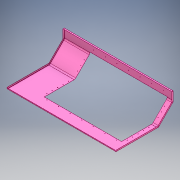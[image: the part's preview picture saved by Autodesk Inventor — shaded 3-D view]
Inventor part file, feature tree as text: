
AUTODESK INVENTOR PART (.ipt)
format: ipt  version: 2018 (Build 220112000, 112)  size: 371,200 bytes
history: native  units: mm
features: sheet_metal_op x13, sketch x10, other x5, hole x4, extrude x1
ambient origin geometry x8: Origin, YZ Plane, XZ Plane, XY Plane, X Axis, Y Axis, Z Axis, Center Point
bodies: Solid1 (feature_tree)
feature tree (33):
  sheet_metal_op  "Face1"
  sheet_metal_op  "Flange1"
  sheet_metal_op  "Flange2"
  extrude  "Extrusion1"  Depth=550.0mm
  sheet_metal_op  "Flange3"
  sheet_metal_op  "Flange4"
  sketch  "Sketch12"  dims[d13=1.6mm]
  sketch  "Sketch13"  dims[d14=0.8mm]
  sketch  "Sketch14"  dims[d15=3.2mm]
  hole  "Hole1"  [1 undecoded]
  hole  "Hole2"  [1 undecoded]
  hole  "Hole3"  [1 undecoded]
  hole  "Hole4"  [1 undecoded]
  sketch  "Sketch1"  dims[d0=1410.0mm d1=550.0mm]
  other  "Plate1"
  sketch  "Sketch2"  dims[d2=1.6mm d3=1.6mm]
  other  "Plate2"
  sheet_metal_op  "Bend1"
  sheet_metal_op  "Corner1"
  sketch  "Sketch3"  dims[d4=0.8mm d5=3.2mm]
  other  "Plate3"
  sheet_metal_op  "Bend2"
  sheet_metal_op  "Corner2"
  sketch  "Sketch4"  dims[d6=1.6mm d7=270.0mm d8=45.0deg d9=30.0mm]
  sketch  "Sketch5"  dims[d10=6.4mm d11=1.6mm]
  other  "Plate4"
  sheet_metal_op  "Bend3"
  sheet_metal_op  "Corner3"
  sketch  "Sketch6"  dims[d12=1.6mm]
  other  "Plate5"
  sheet_metal_op  "Bend4"
  sheet_metal_op  "Corner4"
  sketch  "Sketch15"  dims[d16=1.6mm d17=125.0mm d18=45.0deg d19=30.0mm d20=6.4mm d21=1.6mm d22=1.6mm d23=1000.0mm d24=1000.0mm d25=150.0mm d26=210.0mm d27=0.0mm d28=1.6mm d29=0.8mm d30=3.2mm d31=1.6mm d32=20.0mm d33=90.0deg d34=1.6mm d35=6.4mm d36=1.6mm d37=1.6mm d38=1.6mm d39=0.8mm d40=3.2mm d41=1.6mm d42=20.0mm d43=12.217305mm d44=1.6mm d45=6.4mm d46=1.6mm d47=1.6mm d48=80.0mm d88=15.0mm d89=500.0mm d90=40.0mm d92=150.0mm d93=10.0mm d95=10.0mm d97=40.0mm d99=150.0mm d100=10.0mm d102=10.0mm d104=45.0mm d105=500.0mm d106=40.0mm d108=150.0mm d109=40.0mm d111=150.0mm d114=20.0mm d115=193.5mm d116=30.0mm d118=70.0mm d119=30.0mm d121=70.0mm d124=20.0mm d125=193.5mm d126=30.0mm d128=70.0mm d129=30.0mm d131=70.0mm d134=20.0mm d135=122.0mm d136=20.0mm d138=60.0mm d139=20.0mm d141=60.0mm d144=20.0mm d145=122.0mm d146=20.0mm d148=60.0mm d149=20.0mm d151=60.0mm d154=5.0mm d155=6.0mm d156=7.0mm d157=2.0mm d158=90.0deg d159=1.6mm d160=20.594885mm d161=5.0mm d162=6.0mm d163=7.0mm d164=2.0mm d165=90.0deg d166=1.6mm d167=20.594885mm d168=5.0mm d169=6.0mm d170=7.0mm d171=2.0mm d172=90.0deg d173=1.6mm d174=20.594885mm d175=5.0mm d176=6.0mm d177=7.0mm d178=2.0mm d179=90.0deg d180=1.6mm d181=20.594885mm]
note: 4 required parameter values undecoded (feature->parameter linkage not recoverable at this tier; creation-order binding heuristic only, values carry confidence <= 0.55)
